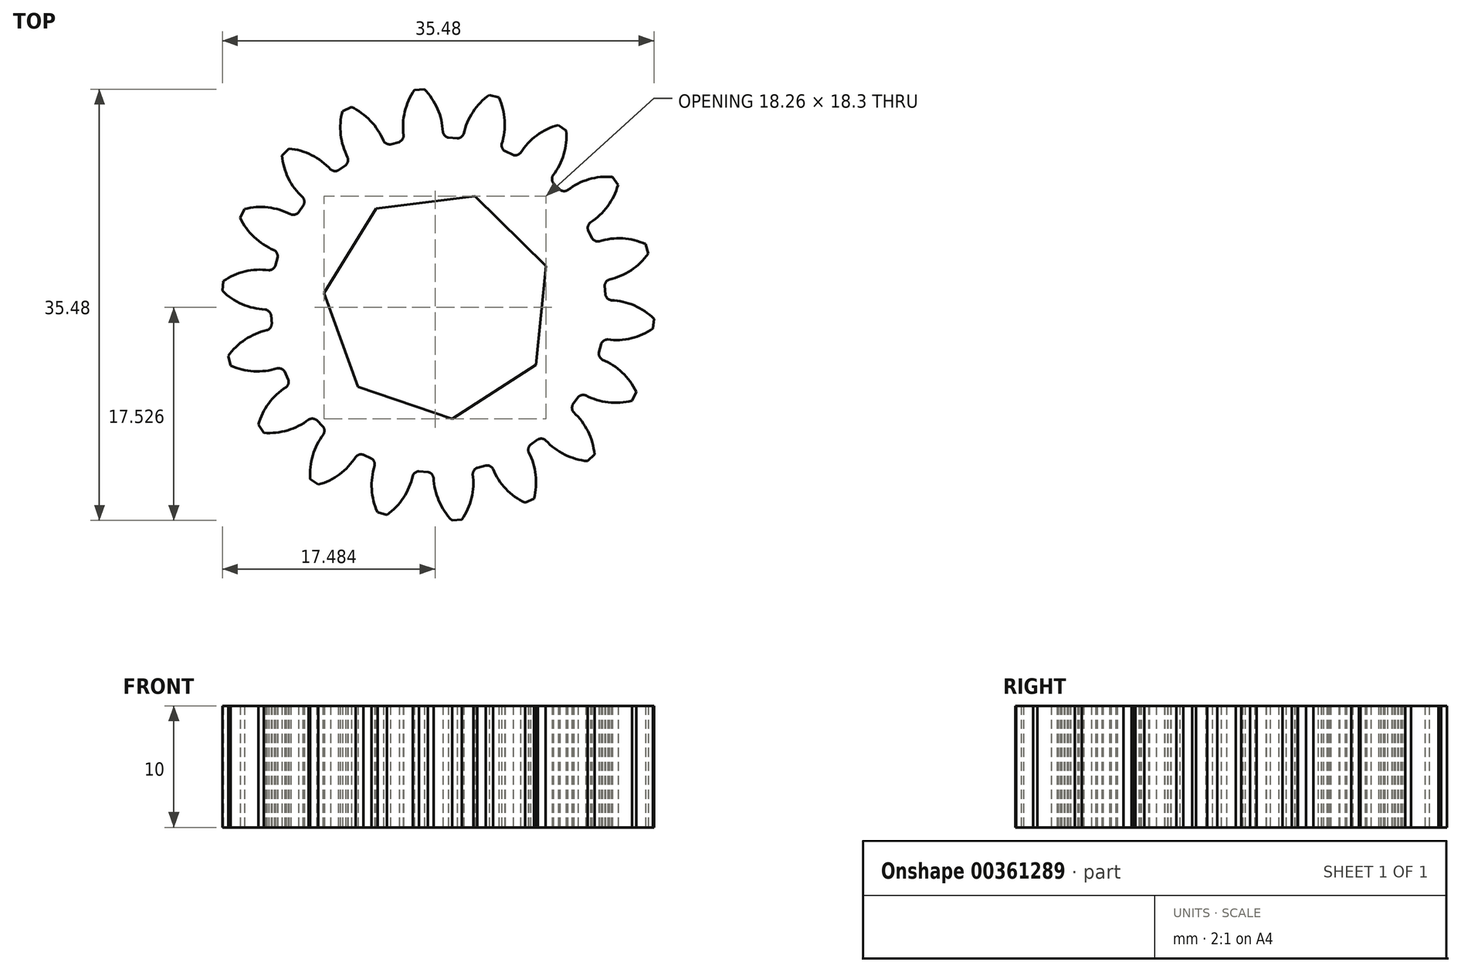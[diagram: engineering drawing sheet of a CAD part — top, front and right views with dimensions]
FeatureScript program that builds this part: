
annotation { "Feature Type Name" : "Feature", "Feature Type Description" : "" }
export const myFeature = defineFeature(function(context is Context, id is Id, definition is map)
    precondition{}
    {
        {
            var Q0;
            Q0=qCreatedBy(makeId("Top.planeOp"),FACE);
            var sketch = newSketch(context, id + "F0", { "sketchPlane" : qUnion([Q0])});
            skPoint(sketch, "E0.center", {"position": v(0, 0) * mm});
            skCircle(sketch, "E1", {"center": v(0, 0) * mm, "radius": 16 * mm, "construction": true});
            skCircle(sketch, "E2", {"center": v(0, 0) * mm, "radius": 13.78 * mm, "construction": true});
            skCircle(sketch, "E3", {"center": v(0, 0) * mm, "radius": 17.78 * mm, "construction": true});
            skCircle(sketch, "E4", {"center": v(0, 0) * mm, "radius": 17 * mm, "construction": true});
            skCircle(sketch, "E5", {"center": v(0, 0) * mm, "radius": 15.05 * mm, "construction": true});
            skLineSegment(sketch, "E6", {"start": v(0, 0) * mm, "end": v(-3.73, 14.64) * mm, "construction": true});
            skLineSegment(sketch, "E7", {"start": v(-3.73, 14.64) * mm, "end": v(-2.95, 12.49) * mm, "construction": true});
            skLineSegment(sketch, "E8", {"start": v(-0.18, 16.5) * mm, "end": v(0.18, 15.5) * mm, "construction": true});
            skLineSegment(sketch, "E9", {"start": v(-6.25, 13.73) * mm, "end": v(0, 0) * mm, "construction": true});
            skLineSegment(sketch, "E10", {"start": v(-6.25, 13.73) * mm, "end": v(-3.81, 10.36) * mm, "construction": true});
            skLineSegment(sketch, "E11", {"start": v(0, 0) * mm, "end": v(0.18, 15.5) * mm, "construction": true});
            skLineSegment(sketch, "E12", {"start": v(0.18, 15.5) * mm, "end": v(0.99, 11.26) * mm, "construction": true});
            skLineSegment(sketch, "E13", {"start": v(0.36, 14.58) * mm, "end": v(0, 0) * mm, "construction": true});
            skLineSegment(sketch, "E14", {"start": v(0.36, 14.58) * mm, "end": v(0.61, 11.2) * mm, "construction": true});
            skLineSegment(sketch, "E15", {"start": v(0, 0) * mm, "end": v(4.85, 17.75) * mm, "construction": true});
            skLineSegment(sketch, "E16", {"start": v(0, 0) * mm, "end": v(-0.18, 16.5) * mm, "construction": true});
            skLineSegment(sketch, "E17", {"start": v(-0.18, 16.5) * mm, "end": v(-2.53, 19.74) * mm, "construction": true});
            skLineSegment(sketch, "E18", {"start": v(-0.18, 16.5) * mm, "end": v(-0.8, 17.37) * mm, "construction": true});
            skArc(sketch, "E19.trimOffspring", {"start": v(-5.42, 14.04) * mm, "mid": v(-5.42, 14.03) * mm, "end": v(-5.42, 14.03) * mm});
            skCircle(sketch, "E20", {"center": v(0, 16) * mm, "radius": 1.4 * mm, "construction": true});
            skLineSegment(sketch, "E21", {"start": v(-1.4, 15.94) * mm, "end": v(0, 0) * mm, "construction": true});
            skArc(sketch, "E22.trimOffspring", {"start": v(0.38, 13.77) * mm, "mid": v(0.03, 15.92) * mm, "end": v(-1.15, 17.74) * mm});
            skArc(sketch, "E23.MirrorCS", {"start": v(-2.77, 13.5) * mm, "mid": v(-2.8, 15.67) * mm, "end": v(-1.95, 17.67) * mm});
            skLineSegment(sketch, "E24", {"start": v(-1.95, 17.67) * mm, "end": v(-1.15, 17.74) * mm});
            skLineSegment(sketch, "E25.1.0", {"start": v(-7.88, 15.94) * mm, "end": v(-7.15, 16.28) * mm});
            skArc(sketch, "E25.1.1", {"start": v(-4.35, 13.08) * mm, "mid": v(-5.41, 14.97) * mm, "end": v(-7.15, 16.28) * mm});
            skArc(sketch, "E25.1.2", {"start": v(-7.22, 11.74) * mm, "mid": v(-7.99, 13.77) * mm, "end": v(-7.88, 15.94) * mm});
            skLineSegment(sketch, "E25.2.0", {"start": v(-12.85, 12.28) * mm, "end": v(-12.28, 12.85) * mm});
            skArc(sketch, "E25.2.1", {"start": v(-8.56, 10.8) * mm, "mid": v(-10.2, 12.21) * mm, "end": v(-12.28, 12.85) * mm});
            skArc(sketch, "E25.2.2", {"start": v(-10.8, 8.56) * mm, "mid": v(-12.21, 10.2) * mm, "end": v(-12.85, 12.28) * mm});
            skLineSegment(sketch, "E25.3.0", {"start": v(-16.28, 7.15) * mm, "end": v(-15.94, 7.88) * mm});
            skArc(sketch, "E25.3.1", {"start": v(-11.74, 7.22) * mm, "mid": v(-13.77, 7.99) * mm, "end": v(-15.94, 7.88) * mm});
            skArc(sketch, "E25.3.2", {"start": v(-13.07, 4.35) * mm, "mid": v(-14.97, 5.42) * mm, "end": v(-16.28, 7.15) * mm});
            skLineSegment(sketch, "E25.4.0", {"start": v(-17.74, 1.15) * mm, "end": v(-17.67, 1.95) * mm});
            skArc(sketch, "E25.4.1", {"start": v(-13.5, 2.77) * mm, "mid": v(-15.67, 2.8) * mm, "end": v(-17.67, 1.95) * mm});
            skArc(sketch, "E25.4.2", {"start": v(-13.77, -0.38) * mm, "mid": v(-15.92, -0.03) * mm, "end": v(-17.74, 1.15) * mm});
            skLineSegment(sketch, "E25.5.0", {"start": v(-17.07, -4.99) * mm, "end": v(-17.27, -4.21) * mm});
            skArc(sketch, "E25.5.1", {"start": v(-13.63, -2.01) * mm, "mid": v(-15.68, -2.73) * mm, "end": v(-17.27, -4.21) * mm});
            skArc(sketch, "E25.5.2", {"start": v(-12.81, -5.07) * mm, "mid": v(-14.95, -5.47) * mm, "end": v(-17.07, -4.99) * mm});
            skLineSegment(sketch, "E25.6.0", {"start": v(-14.33, -10.53) * mm, "end": v(-14.8, -9.86) * mm});
            skArc(sketch, "E25.6.1", {"start": v(-12.12, -6.56) * mm, "mid": v(-13.8, -7.93) * mm, "end": v(-14.8, -9.86) * mm});
            skArc(sketch, "E25.6.2", {"start": v(-10.3, -9.15) * mm, "mid": v(-12.17, -10.26) * mm, "end": v(-14.33, -10.53) * mm});
            skLineSegment(sketch, "E25.7.0", {"start": v(-9.87, -14.8) * mm, "end": v(-10.53, -14.33) * mm});
            skArc(sketch, "E25.7.1", {"start": v(-9.15, -10.3) * mm, "mid": v(-10.26, -12.17) * mm, "end": v(-10.53, -14.33) * mm});
            skArc(sketch, "E25.7.2", {"start": v(-6.56, -12.12) * mm, "mid": v(-7.93, -13.8) * mm, "end": v(-9.87, -14.8) * mm});
            skLineSegment(sketch, "E25.8.0", {"start": v(-4.21, -17.27) * mm, "end": v(-5, -17.07) * mm});
            skArc(sketch, "E25.8.1", {"start": v(-5.07, -12.81) * mm, "mid": v(-5.47, -14.95) * mm, "end": v(-5, -17.07) * mm});
            skArc(sketch, "E25.8.2", {"start": v(-2.02, -13.63) * mm, "mid": v(-2.73, -15.68) * mm, "end": v(-4.21, -17.27) * mm});
            skLineSegment(sketch, "E25.9.0", {"start": v(1.95, -17.67) * mm, "end": v(1.15, -17.74) * mm});
            skArc(sketch, "E25.9.1", {"start": v(-0.38, -13.77) * mm, "mid": v(-0.03, -15.92) * mm, "end": v(1.15, -17.74) * mm});
            skArc(sketch, "E25.9.2", {"start": v(2.77, -13.5) * mm, "mid": v(2.8, -15.67) * mm, "end": v(1.95, -17.67) * mm});
            skLineSegment(sketch, "E25.10.0", {"start": v(7.88, -15.94) * mm, "end": v(7.15, -16.28) * mm});
            skArc(sketch, "E25.10.1", {"start": v(4.35, -13.08) * mm, "mid": v(5.41, -14.97) * mm, "end": v(7.15, -16.28) * mm});
            skArc(sketch, "E25.10.2", {"start": v(7.22, -11.74) * mm, "mid": v(7.99, -13.77) * mm, "end": v(7.88, -15.94) * mm});
            skLineSegment(sketch, "E25.11.0", {"start": v(12.85, -12.28) * mm, "end": v(12.28, -12.85) * mm});
            skArc(sketch, "E25.11.1", {"start": v(8.56, -10.8) * mm, "mid": v(10.2, -12.21) * mm, "end": v(12.28, -12.85) * mm});
            skArc(sketch, "E25.11.2", {"start": v(10.8, -8.56) * mm, "mid": v(12.21, -10.2) * mm, "end": v(12.85, -12.28) * mm});
            skLineSegment(sketch, "E25.12.0", {"start": v(16.28, -7.15) * mm, "end": v(15.94, -7.88) * mm});
            skArc(sketch, "E25.12.1", {"start": v(11.74, -7.22) * mm, "mid": v(13.77, -7.99) * mm, "end": v(15.94, -7.88) * mm});
            skArc(sketch, "E25.12.2", {"start": v(13.07, -4.35) * mm, "mid": v(14.97, -5.42) * mm, "end": v(16.28, -7.15) * mm});
            skLineSegment(sketch, "E25.13.0", {"start": v(17.74, -1.15) * mm, "end": v(17.67, -1.95) * mm});
            skArc(sketch, "E25.13.1", {"start": v(13.5, -2.77) * mm, "mid": v(15.67, -2.8) * mm, "end": v(17.67, -1.95) * mm});
            skArc(sketch, "E25.13.2", {"start": v(13.77, 0.38) * mm, "mid": v(15.92, 0.03) * mm, "end": v(17.74, -1.15) * mm});
            skLineSegment(sketch, "E25.14.0", {"start": v(17.07, 4.99) * mm, "end": v(17.27, 4.21) * mm});
            skArc(sketch, "E25.14.1", {"start": v(13.63, 2.01) * mm, "mid": v(15.68, 2.73) * mm, "end": v(17.27, 4.21) * mm});
            skArc(sketch, "E25.14.2", {"start": v(12.81, 5.07) * mm, "mid": v(14.95, 5.47) * mm, "end": v(17.07, 4.99) * mm});
            skLineSegment(sketch, "E25.15.0", {"start": v(14.33, 10.53) * mm, "end": v(14.8, 9.86) * mm});
            skArc(sketch, "E25.15.1", {"start": v(12.12, 6.56) * mm, "mid": v(13.8, 7.93) * mm, "end": v(14.8, 9.86) * mm});
            skArc(sketch, "E25.15.2", {"start": v(10.3, 9.15) * mm, "mid": v(12.17, 10.26) * mm, "end": v(14.33, 10.53) * mm});
            skLineSegment(sketch, "E25.16.0", {"start": v(9.87, 14.8) * mm, "end": v(10.53, 14.33) * mm});
            skArc(sketch, "E25.16.1", {"start": v(9.15, 10.3) * mm, "mid": v(10.26, 12.17) * mm, "end": v(10.53, 14.33) * mm});
            skArc(sketch, "E25.16.2", {"start": v(6.56, 12.12) * mm, "mid": v(7.93, 13.8) * mm, "end": v(9.87, 14.8) * mm});
            skLineSegment(sketch, "E25.17.0", {"start": v(4.21, 17.27) * mm, "end": v(5, 17.07) * mm});
            skArc(sketch, "E25.17.1", {"start": v(5.07, 12.81) * mm, "mid": v(5.47, 14.95) * mm, "end": v(5, 17.07) * mm});
            skArc(sketch, "E25.17.2", {"start": v(2.02, 13.63) * mm, "mid": v(2.73, 15.68) * mm, "end": v(4.21, 17.27) * mm});
            skCircle(sketch, "E26", {"center": v(0.38, 13.77) * mm, "radius": 0.45 * mm, "construction": true});
            skCircle(sketch, "E27", {"center": v(2.02, 13.63) * mm, "radius": 0.45 * mm, "construction": true});
            skArc(sketch, "E28", {"start": v(0.38, 14.22) * mm, "mid": v(0.54, 13.92) * mm, "end": v(0.83, 13.75) * mm});
            skArc(sketch, "E29", {"start": v(1.57, 13.7) * mm, "mid": v(1.89, 13.8) * mm, "end": v(2.1, 14.08) * mm});
            skLineSegment(sketch, "E30", {"start": v(0.83, 13.75) * mm, "end": v(1.57, 13.7) * mm});
            skArc(sketch, "E31.1.0", {"start": v(-4.5, 13.5) * mm, "mid": v(-4.25, 13.27) * mm, "end": v(-3.92, 13.21) * mm});
            skArc(sketch, "E31.1.1", {"start": v(-3.2, 13.4) * mm, "mid": v(-2.95, 13.62) * mm, "end": v(-2.85, 13.94) * mm});
            skLineSegment(sketch, "E31.1.2", {"start": v(-3.92, 13.21) * mm, "end": v(-3.2, 13.4) * mm});
            skArc(sketch, "E31.2.0", {"start": v(-8.85, 11.14) * mm, "mid": v(-8.54, 11.01) * mm, "end": v(-8.2, 11.07) * mm});
            skArc(sketch, "E31.2.1", {"start": v(-7.6, 11.5) * mm, "mid": v(-7.43, 11.79) * mm, "end": v(-7.44, 12.13) * mm});
            skLineSegment(sketch, "E31.2.2", {"start": v(-8.2, 11.07) * mm, "end": v(-7.6, 11.5) * mm});
            skArc(sketch, "E31.3.0", {"start": v(-12.13, 7.44) * mm, "mid": v(-11.79, 7.43) * mm, "end": v(-11.5, 7.6) * mm});
            skArc(sketch, "E31.3.1", {"start": v(-11.07, 8.2) * mm, "mid": v(-11.01, 8.54) * mm, "end": v(-11.14, 8.85) * mm});
            skLineSegment(sketch, "E31.3.2", {"start": v(-11.5, 7.6) * mm, "end": v(-11.07, 8.2) * mm});
            skArc(sketch, "E31.4.0", {"start": v(-13.94, 2.85) * mm, "mid": v(-13.62, 2.95) * mm, "end": v(-13.4, 3.21) * mm});
            skArc(sketch, "E31.4.1", {"start": v(-13.21, 3.92) * mm, "mid": v(-13.27, 4.26) * mm, "end": v(-13.5, 4.5) * mm});
            skLineSegment(sketch, "E31.4.2", {"start": v(-13.4, 3.21) * mm, "end": v(-13.21, 3.92) * mm});
            skArc(sketch, "E31.5.0", {"start": v(-14.07, -2.1) * mm, "mid": v(-13.8, -1.89) * mm, "end": v(-13.7, -1.57) * mm});
            skArc(sketch, "E31.5.1", {"start": v(-13.75, -0.83) * mm, "mid": v(-13.92, -0.54) * mm, "end": v(-14.23, -0.38) * mm});
            skLineSegment(sketch, "E31.5.2", {"start": v(-13.7, -1.57) * mm, "end": v(-13.75, -0.83) * mm});
            skArc(sketch, "E31.6.0", {"start": v(-12.51, -6.78) * mm, "mid": v(-12.33, -6.5) * mm, "end": v(-12.33, -6.15) * mm});
            skArc(sketch, "E31.6.1", {"start": v(-12.64, -5.49) * mm, "mid": v(-12.9, -5.27) * mm, "end": v(-13.24, -5.22) * mm});
            skLineSegment(sketch, "E31.6.2", {"start": v(-12.33, -6.15) * mm, "end": v(-12.64, -5.49) * mm});
            skArc(sketch, "E31.7.0", {"start": v(-9.44, -10.65) * mm, "mid": v(-9.36, -10.32) * mm, "end": v(-9.48, -10) * mm});
            skArc(sketch, "E31.7.1", {"start": v(-10, -9.48) * mm, "mid": v(-10.32, -9.36) * mm, "end": v(-10.65, -9.44) * mm});
            skLineSegment(sketch, "E31.7.2", {"start": v(-9.48, -10) * mm, "end": v(-10, -9.48) * mm});
            skArc(sketch, "E31.8.0", {"start": v(-5.23, -13.23) * mm, "mid": v(-5.27, -12.9) * mm, "end": v(-5.49, -12.64) * mm});
            skArc(sketch, "E31.8.1", {"start": v(-6.16, -12.33) * mm, "mid": v(-6.5, -12.33) * mm, "end": v(-6.78, -12.51) * mm});
            skLineSegment(sketch, "E31.8.2", {"start": v(-5.49, -12.64) * mm, "end": v(-6.16, -12.33) * mm});
            skArc(sketch, "E31.9.0", {"start": v(-0.38, -14.22) * mm, "mid": v(-0.54, -13.92) * mm, "end": v(-0.83, -13.75) * mm});
            skArc(sketch, "E31.9.1", {"start": v(-1.57, -13.7) * mm, "mid": v(-1.89, -13.8) * mm, "end": v(-2.1, -14.08) * mm});
            skLineSegment(sketch, "E31.9.2", {"start": v(-0.83, -13.75) * mm, "end": v(-1.57, -13.7) * mm});
            skArc(sketch, "E31.10.0", {"start": v(4.5, -13.5) * mm, "mid": v(4.25, -13.27) * mm, "end": v(3.92, -13.21) * mm});
            skArc(sketch, "E31.10.1", {"start": v(3.2, -13.4) * mm, "mid": v(2.95, -13.62) * mm, "end": v(2.85, -13.94) * mm});
            skLineSegment(sketch, "E31.10.2", {"start": v(3.92, -13.21) * mm, "end": v(3.2, -13.4) * mm});
            skArc(sketch, "E31.11.0", {"start": v(8.85, -11.14) * mm, "mid": v(8.54, -11.01) * mm, "end": v(8.2, -11.07) * mm});
            skArc(sketch, "E31.11.1", {"start": v(7.6, -11.5) * mm, "mid": v(7.43, -11.79) * mm, "end": v(7.44, -12.13) * mm});
            skLineSegment(sketch, "E31.11.2", {"start": v(8.2, -11.07) * mm, "end": v(7.6, -11.5) * mm});
            skArc(sketch, "E31.12.0", {"start": v(12.13, -7.44) * mm, "mid": v(11.79, -7.43) * mm, "end": v(11.5, -7.6) * mm});
            skArc(sketch, "E31.12.1", {"start": v(11.07, -8.2) * mm, "mid": v(11.01, -8.54) * mm, "end": v(11.14, -8.85) * mm});
            skLineSegment(sketch, "E31.12.2", {"start": v(11.5, -7.6) * mm, "end": v(11.07, -8.2) * mm});
            skArc(sketch, "E31.13.0", {"start": v(13.94, -2.85) * mm, "mid": v(13.62, -2.95) * mm, "end": v(13.4, -3.21) * mm});
            skArc(sketch, "E31.13.1", {"start": v(13.21, -3.92) * mm, "mid": v(13.27, -4.26) * mm, "end": v(13.5, -4.5) * mm});
            skLineSegment(sketch, "E31.13.2", {"start": v(13.4, -3.21) * mm, "end": v(13.21, -3.92) * mm});
            skArc(sketch, "E31.14.0", {"start": v(14.07, 2.1) * mm, "mid": v(13.8, 1.89) * mm, "end": v(13.7, 1.57) * mm});
            skArc(sketch, "E31.14.1", {"start": v(13.75, 0.83) * mm, "mid": v(13.92, 0.54) * mm, "end": v(14.23, 0.38) * mm});
            skLineSegment(sketch, "E31.14.2", {"start": v(13.7, 1.57) * mm, "end": v(13.75, 0.83) * mm});
            skArc(sketch, "E31.15.0", {"start": v(12.51, 6.78) * mm, "mid": v(12.33, 6.5) * mm, "end": v(12.33, 6.15) * mm});
            skArc(sketch, "E31.15.1", {"start": v(12.64, 5.49) * mm, "mid": v(12.9, 5.27) * mm, "end": v(13.24, 5.22) * mm});
            skLineSegment(sketch, "E31.15.2", {"start": v(12.33, 6.15) * mm, "end": v(12.64, 5.49) * mm});
            skArc(sketch, "E31.16.0", {"start": v(9.44, 10.65) * mm, "mid": v(9.36, 10.32) * mm, "end": v(9.48, 10) * mm});
            skArc(sketch, "E31.16.1", {"start": v(10, 9.48) * mm, "mid": v(10.32, 9.36) * mm, "end": v(10.65, 9.44) * mm});
            skLineSegment(sketch, "E31.16.2", {"start": v(9.48, 10) * mm, "end": v(10, 9.48) * mm});
            skArc(sketch, "E31.17.0", {"start": v(5.23, 13.23) * mm, "mid": v(5.27, 12.9) * mm, "end": v(5.49, 12.64) * mm});
            skArc(sketch, "E31.17.1", {"start": v(6.16, 12.33) * mm, "mid": v(6.5, 12.33) * mm, "end": v(6.78, 12.51) * mm});
            skLineSegment(sketch, "E31.17.2", {"start": v(5.49, 12.64) * mm, "end": v(6.16, 12.33) * mm});
            skLineSegment(sketch, "E32", {"start": v(-9.42, 11.47) * mm, "end": v(0, 0) * mm, "construction": true});
            skCircle(sketch, "E33.cCircle", {"center": v(0, 0) * mm, "radius": 8.5 * mm, "construction": true});
            skLineSegment(sketch, "E33.0", {"start": v(8.04, -4.94) * mm, "end": v(1.15, -9.36) * mm});
            skLineSegment(sketch, "E33.1", {"start": v(1.15, -9.36) * mm, "end": v(-6.6, -6.74) * mm});
            skLineSegment(sketch, "E33.2", {"start": v(-6.6, -6.74) * mm, "end": v(-9.38, 0.96) * mm});
            skLineSegment(sketch, "E33.3", {"start": v(-9.38, 0.96) * mm, "end": v(-5.1, 7.94) * mm});
            skLineSegment(sketch, "E33.4", {"start": v(-5.1, 7.94) * mm, "end": v(3.03, 8.94) * mm});
            skLineSegment(sketch, "E33.5", {"start": v(3.03, 8.94) * mm, "end": v(8.87, 3.2) * mm});
            skLineSegment(sketch, "E33.6", {"start": v(8.87, 3.2) * mm, "end": v(8.04, -4.94) * mm});
            skPoint(sketch, "E33.0.midPoint", {"position": v(4.6, -7.15) * mm});
            skSolve(sketch);
        }
        {
            var Q0;
            {var subQ56=sQuery(id+"F0.wireOp",EDGE,"E24");Q0=makeQuery(id+"F0.imprint","IMPRINT",FACE,{"disambiguationData":[TD([[makeQuery(id+"F0.imprint","IMPRINT",EDGE,{"derivedFrom":subQ56}),-1.0]])]});}
            extrude(context, id + "F1", {"entities" : qUnion([Q0]), "depth" : 10 * mm});
        }
    });
